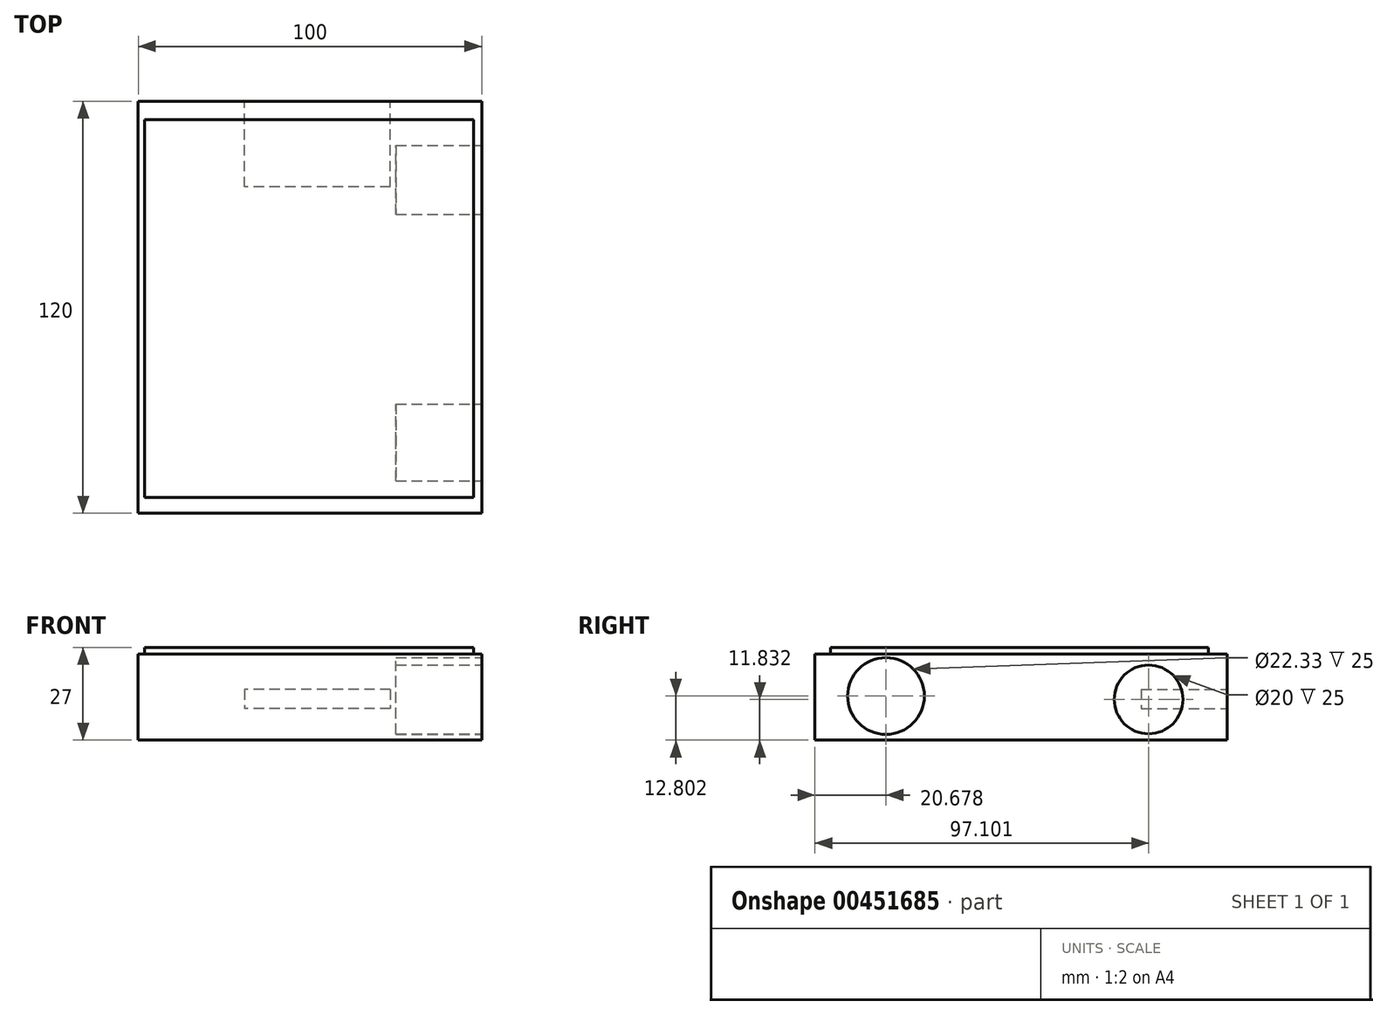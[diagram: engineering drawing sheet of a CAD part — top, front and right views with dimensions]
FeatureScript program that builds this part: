
annotation { "Feature Type Name" : "Feature", "Feature Type Description" : "" }
export const myFeature = defineFeature(function(context is Context, id is Id, definition is map)
    precondition{}
    {
        {
            var Q0;
            Q0=qCreatedBy(makeId("Top.planeOp"),FACE);
            var sketch = newSketch(context, id + "F0", { "sketchPlane" : qUnion([Q0])});
            skLineSegment(sketch, "E0.bottom", {"start": v(-54.96, 53.74) * mm, "end": v(45.04, 53.74) * mm});
            skLineSegment(sketch, "E0.top", {"start": v(-54.96, -66.26) * mm, "end": v(45.04, -66.26) * mm});
            skLineSegment(sketch, "E0.left", {"start": v(-54.96, 53.74) * mm, "end": v(-54.96, -66.26) * mm});
            skLineSegment(sketch, "E0.right", {"start": v(45.04, 53.74) * mm, "end": v(45.04, -66.26) * mm});
            skSolve(sketch);
        }
        {
            var Q0;
            Q0 = qSketchRegion(id + "F0", true);
            extrude(context, id + "F1", {"entities" : qUnion([Q0]), "depth" : 25 * mm});
        }
        {
            var Q0;
            Q0=makeQuery(id+"F1.opExtrude","SWEPT_FACE",FACE,{"disambiguationData":[OSD([sQuery(id+"F0.wireOp",EDGE,"E0.right")])]});
            var sketch = newSketch(context, id + "F2", { "sketchPlane" : qUnion([Q0])});
            skCircle(sketch, "E1", {"center": v(-45.58, 12.8) * mm, "radius": 11.17 * mm});
            skSolve(sketch);
        }
        {
            var Q0;
            Q0 = qSketchRegion(id + "F2", true);
            extrude(context, id + "F3", {"entities" : qUnion([Q0]), "operationType" : NewBodyOperationType.REMOVE, "oppositeDirection" : true, "depth" : 25 * mm});
        }
        {
            var Q0;
            Q0=makeQuery(id+"F1.opExtrude","SWEPT_FACE",FACE,{"disambiguationData":[OSD([sQuery(id+"F0.wireOp",EDGE,"E0.right")])]});
            var sketch = newSketch(context, id + "F4", { "sketchPlane" : qUnion([Q0])});
            skCircle(sketch, "E2", {"center": v(30.84, 11.83) * mm, "radius": 10 * mm});
            skSolve(sketch);
        }
        {
            var Q0;
            Q0=makeQuery(id+"F4.imprint","IMPRINT",FACE,{"disambiguationData":[TD([[makeQuery(id+"F4.imprint","IMPRINT",EDGE,{"derivedFrom":sQuery(id+"F4.wireOp",EDGE,"E2")}),1.0]])]});
            extrude(context, id + "F5", {"entities" : qUnion([Q0]), "operationType" : NewBodyOperationType.REMOVE, "oppositeDirection" : true, "depth" : 25 * mm});
        }
        {
            var Q0;
            Q0=makeQuery(id+"F1.opExtrude","SWEPT_FACE",FACE,{"disambiguationData":[OSD([sQuery(id+"F0.wireOp",EDGE,"E0.bottom")])]});
            var sketch = newSketch(context, id + "F6", { "sketchPlane" : qUnion([Q0])});
            skLineSegment(sketch, "E3.bottom", {"start": v(-18.43, 14.74) * mm, "end": v(24.05, 14.74) * mm});
            skLineSegment(sketch, "E3.top", {"start": v(-18.43, 9.12) * mm, "end": v(24.05, 9.12) * mm});
            skLineSegment(sketch, "E3.left", {"start": v(-18.43, 14.74) * mm, "end": v(-18.43, 9.12) * mm});
            skLineSegment(sketch, "E3.right", {"start": v(24.05, 14.74) * mm, "end": v(24.05, 9.12) * mm});
            skSolve(sketch);
        }
        {
            var Q0;
            Q0=makeQuery(id+"F1.opExtrude","CAP_FACE",FACE,{"disambiguationData":[OSD([sQuery(id+"F0.wireOp",EDGE,"E0.bottom"),sQuery(id+"F0.wireOp",EDGE,"E0.top"),sQuery(id+"F0.wireOp",EDGE,"E0.left"),sQuery(id+"F0.wireOp",EDGE,"E0.right")])],"isStart":false});
            var sketch = newSketch(context, id + "F7", { "sketchPlane" : qUnion([Q0])});
            skLineSegment(sketch, "E4.bottom", {"start": v(-53.15, 48.3) * mm, "end": v(42.67, 48.3) * mm});
            skLineSegment(sketch, "E4.top", {"start": v(-53.15, -61.68) * mm, "end": v(42.67, -61.68) * mm});
            skLineSegment(sketch, "E4.left", {"start": v(-53.15, 48.3) * mm, "end": v(-53.15, -61.68) * mm});
            skLineSegment(sketch, "E4.right", {"start": v(42.67, 48.3) * mm, "end": v(42.67, -61.68) * mm});
            skSolve(sketch);
        }
        {
            var Q0;
            Q0=makeQuery(id+"F7.imprint","IMPRINT",FACE,{"disambiguationData":[TD([[makeQuery(id+"F7.imprint","IMPRINT",EDGE,{"derivedFrom":sQuery(id+"F7.wireOp",EDGE,"E4.bottom")}),-1.0]])]});
            extrude(context, id + "F8", {"entities" : qUnion([Q0]), "operationType" : NewBodyOperationType.ADD, "depth" : 2 * mm});
        }
        {
            var Q0;
            Q0=makeQuery(id+"F6.imprint","IMPRINT",FACE,{"disambiguationData":[TD([[makeQuery(id+"F6.imprint","IMPRINT",EDGE,{"derivedFrom":sQuery(id+"F6.wireOp",EDGE,"E3.bottom")}),-1.0]])]});
            extrude(context, id + "F9", {"entities" : qUnion([Q0]), "operationType" : NewBodyOperationType.REMOVE, "oppositeDirection" : true, "depth" : 25 * mm});
        }
    });
